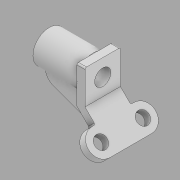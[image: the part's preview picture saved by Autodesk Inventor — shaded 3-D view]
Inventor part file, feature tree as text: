
AUTODESK INVENTOR PART (.ipt)
format: ipt  version: 2020 (Build 240168000, 168)  size: 206,336 bytes
history: native  units: mm
features: sketch x6, projected_geometry x4, extrude x3, other x2, hole x2, fillet x1
ambient origin geometry x8: Origin, YZ Plane, XZ Plane, XY Plane, X Axis, Y Axis, Z Axis, Center Point
bodies: Body1 (feature_tree)
feature tree (18):
  other  "Sólido1"
  extrude  "Extrusión1"  Depth=35.0mm
  extrude  "Extrusión2"  Depth=25.0mm
  extrude  "Extrusión3"  TaperAngle=45.0deg  [1 undecoded]
  other  "Nervio1"
  hole  "Agujero1"  [1 undecoded]
  hole  "Agujero2"  [1 undecoded]
  fillet  "Empalme1"  Radius=83.0mm
  sketch  "Boceto1"  dims[d0=16.0mm d3=35.0mm]
  sketch  "Boceto2"  dims[d5=25.0mm d6=25.0mm]
  projected_geometry  "Contorno proyectado1"
  sketch  "Boceto3"  dims[d7=70.0mm d10=45.0deg]
  sketch  "Boceto4"  dims[d11=0.0mm d12=70.0mm d13=0.0mm]
  projected_geometry  "Contorno proyectado2"
  projected_geometry  "Contorno proyectado3"
  projected_geometry  "Contorno proyectado4"
  sketch  "Boceto5"  dims[d14=64.0mm d15=106.0mm d16=0.0mm d17=83.0mm]
  sketch  "Boceto6"  dims[d18=41.5mm d19=25.0mm d20=10.0mm d21=0.0mm d22=25.0mm d23=7.0mm d24=1.0mm d25=16.0mm d26=0.0mm d27=0.0mm d28=1.0mm d29=1.0mm d30=32.0mm d31=6.0mm d32=38.1mm d33=2.54mm d34=90.0deg d35=38.1mm d36=0.0mm d37=25.0mm d38=6.0mm d39=38.1mm d40=2.54mm d41=90.0deg d42=38.1mm d43=0.0mm d44=45.0deg d45=3.0mm d46=32.0mm]
note: 3 required parameter values undecoded (feature->parameter linkage not recoverable at this tier; creation-order binding heuristic only, values carry confidence <= 0.55)
